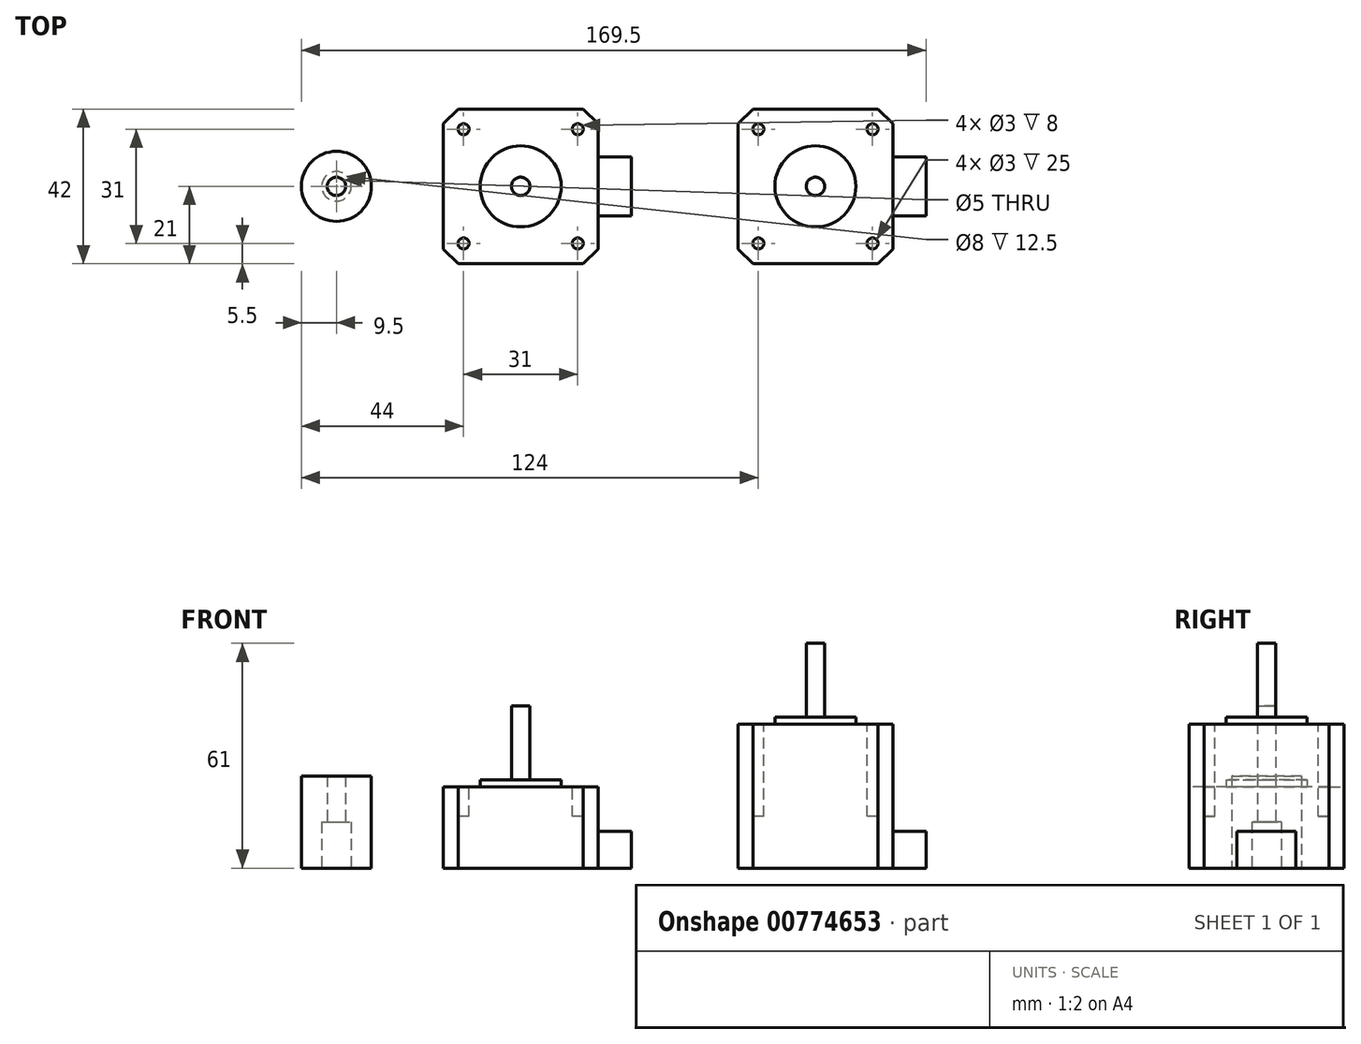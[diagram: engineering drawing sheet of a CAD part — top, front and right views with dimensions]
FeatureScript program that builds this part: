
annotation { "Feature Type Name" : "Feature", "Feature Type Description" : "" }
export const myFeature = defineFeature(function(context is Context, id is Id, definition is map)
    precondition{}
    {
        {
            var Q0;
            Q0=qCreatedBy(makeId("Top.planeOp"),FACE);
            var sketch = newSketch(context, id + "F0", { "sketchPlane" : qUnion([Q0])});
            skLineSegment(sketch, "E0", {"start": v(-21, 17) * mm, "end": v(-21, -17) * mm});
            skLineSegment(sketch, "E1", {"start": v(-21, -17) * mm, "end": v(-17, -21) * mm});
            skLineSegment(sketch, "E2", {"start": v(-17, -21) * mm, "end": v(17, -21) * mm});
            skLineSegment(sketch, "E3", {"start": v(21, -17) * mm, "end": v(17, -21) * mm});
            skLineSegment(sketch, "E4", {"start": v(21, -17) * mm, "end": v(21, 17) * mm});
            skLineSegment(sketch, "E5", {"start": v(21, 17) * mm, "end": v(17, 21) * mm});
            skLineSegment(sketch, "E6", {"start": v(17, 21) * mm, "end": v(-17, 21) * mm});
            skLineSegment(sketch, "E7", {"start": v(-21, 17) * mm, "end": v(-17, 21) * mm});
            skSolve(sketch);
        }
        {
            var Q0;
            Q0=makeQuery(id+"F0.imprint","IMPRINT",FACE,{"disambiguationData":[TD([[makeQuery(id+"F0.imprint","IMPRINT",EDGE,{"derivedFrom":sQuery(id+"F0.wireOp",EDGE,"E0")}),1.0]])]});
            extrude(context, id + "F1", {"entities" : qUnion([Q0]), "depth" : 39 * mm, "offsetDistance" : 25 * mm});
        }
        {
            var Q0;
            Q0=makeQuery(id+"F1.opExtrude","CAP_FACE",FACE,{"disambiguationData":[OSD([sQuery(id+"F0.wireOp",EDGE,"E0"),sQuery(id+"F0.wireOp",EDGE,"E1"),sQuery(id+"F0.wireOp",EDGE,"E2"),sQuery(id+"F0.wireOp",EDGE,"E3"),sQuery(id+"F0.wireOp",EDGE,"E4"),sQuery(id+"F0.wireOp",EDGE,"E5"),sQuery(id+"F0.wireOp",EDGE,"E6"),sQuery(id+"F0.wireOp",EDGE,"E7")])],"isStart":false});
            var sketch = newSketch(context, id + "F2", { "sketchPlane" : qUnion([Q0])});
            skCircle(sketch, "E8", {"center": v(0, 0) * mm, "radius": 11 * mm});
            skSolve(sketch);
        }
        {
            var Q0;
            Q0 = qSketchRegion(id + "F2", true);
            extrude(context, id + "F3", {"entities" : qUnion([Q0]), "operationType" : NewBodyOperationType.ADD, "depth" : 2 * mm, "offsetDistance" : 25 * mm});
        }
        {
            var Q0;
            Q0=makeQuery(id+"F3.opExtrude","CAP_FACE",FACE,{"disambiguationData":[OSD([sQuery(id+"F2.wireOp",EDGE,"E8")])],"isStart":false});
            var sketch = newSketch(context, id + "F4", { "sketchPlane" : qUnion([Q0])});
            skCircle(sketch, "E9", {"center": v(0, 0) * mm, "radius": 2.5 * mm});
            skSolve(sketch);
        }
        {
            var Q0;
            Q0 = qSketchRegion(id + "F4", true);
            extrude(context, id + "F5", {"entities" : qUnion([Q0]), "operationType" : NewBodyOperationType.ADD, "depth" : 20 * mm, "offsetDistance" : 25 * mm});
        }
        {
            var Q0;
            Q0=makeQuery(id+"F1.opExtrude","SWEPT_FACE",FACE,{"disambiguationData":[OSD([sQuery(id+"F0.wireOp",EDGE,"E4")])]});
            var sketch = newSketch(context, id + "F6", { "sketchPlane" : qUnion([Q0])});
            skLineSegment(sketch, "E10.bottom", {"start": v(-8, 0) * mm, "end": v(8, 0) * mm});
            skLineSegment(sketch, "E10.top", {"start": v(-8, 10) * mm, "end": v(8, 10) * mm});
            skLineSegment(sketch, "E10.left", {"start": v(-8, 0) * mm, "end": v(-8, 10) * mm});
            skLineSegment(sketch, "E10.right", {"start": v(8, 0) * mm, "end": v(8, 10) * mm});
            skSolve(sketch);
        }
        {
            var Q0;
            Q0 = qSketchRegion(id + "F6", true);
            extrude(context, id + "F7", {"entities" : qUnion([Q0]), "operationType" : NewBodyOperationType.ADD, "depth" : 9 * mm, "offsetDistance" : 25 * mm});
        }
        {
            var Q0;
            Q0=makeQuery(id+"F1.opExtrude","SWEPT_BODY",BODY,{"disambiguationData":[OSD([sQuery(id+"F0.wireOp",EDGE,"E0"),sQuery(id+"F0.wireOp",EDGE,"E1"),sQuery(id+"F0.wireOp",EDGE,"E2"),sQuery(id+"F0.wireOp",EDGE,"E3"),sQuery(id+"F0.wireOp",EDGE,"E4"),sQuery(id+"F0.wireOp",EDGE,"E5"),sQuery(id+"F0.wireOp",EDGE,"E6"),sQuery(id+"F0.wireOp",EDGE,"E7")])]});
            transform(context, id + "F8", {"entities" : qUnion([Q0]), "transformType" : TransformType.TRANSLATION_3D, "dx" : 82.6 * mm, "dy" : 0 * mm, "dz" : 0 * mm, "makeCopy" : true});
        }
        {
            var Q0;
            Q0=makeQuery(id+"F8.opPattern","COPY",BODY,{"derivedFrom":makeQuery(id+"F1.opExtrude","SWEPT_BODY",BODY,{"disambiguationData":[OSD([sQuery(id+"F0.wireOp",EDGE,"E0"),sQuery(id+"F0.wireOp",EDGE,"E1"),sQuery(id+"F0.wireOp",EDGE,"E2"),sQuery(id+"F0.wireOp",EDGE,"E3"),sQuery(id+"F0.wireOp",EDGE,"E4"),sQuery(id+"F0.wireOp",EDGE,"E5"),sQuery(id+"F0.wireOp",EDGE,"E6"),sQuery(id+"F0.wireOp",EDGE,"E7")])]}),"instanceName":"1"});
            deleteBodies(context, id + "F9", {"entities" : qUnion([Q0])});
        }
        {
            var Q0;
            Q0=makeQuery(id+"F1.opExtrude","SWEPT_BODY",BODY,{"disambiguationData":[OSD([sQuery(id+"F0.wireOp",EDGE,"E0"),sQuery(id+"F0.wireOp",EDGE,"E1"),sQuery(id+"F0.wireOp",EDGE,"E2"),sQuery(id+"F0.wireOp",EDGE,"E3"),sQuery(id+"F0.wireOp",EDGE,"E4"),sQuery(id+"F0.wireOp",EDGE,"E5"),sQuery(id+"F0.wireOp",EDGE,"E6"),sQuery(id+"F0.wireOp",EDGE,"E7")])]});
            var Q1;
            Q1=sQuery(id+"F11.wireOp",EDGE,"E11");
            var Q2;
            Q2=qCreatedBy(makeId("Right.planeOp"),FACE);
            transform(context, id + "F10", {"entities" : qUnion([Q0]), "transformType" : TransformType.TRANSLATION_DISTANCE, "transformDirection" : qUnion([Q2]), "distance" : 80 * mm, "makeCopy" : false});
        }
        {
            var Q0;
            Q0=qCreatedBy(makeId("Top.planeOp"),FACE);
            var sketch = newSketch(context, id + "F11", { "sketchPlane" : qUnion([Q0])});
            skLineSegment(sketch, "E11", {"start": v(-21, 17) * mm, "end": v(-21, -17) * mm});
            skLineSegment(sketch, "E12", {"start": v(-21, -17) * mm, "end": v(-17, -21) * mm});
            skLineSegment(sketch, "E13", {"start": v(-17, -21) * mm, "end": v(17, -21) * mm});
            skLineSegment(sketch, "E14", {"start": v(21, -17) * mm, "end": v(17, -21) * mm});
            skLineSegment(sketch, "E15", {"start": v(21, -17) * mm, "end": v(21, 17) * mm});
            skLineSegment(sketch, "E16", {"start": v(21, 17) * mm, "end": v(17, 21) * mm});
            skLineSegment(sketch, "E17", {"start": v(17, 21) * mm, "end": v(-17, 21) * mm});
            skLineSegment(sketch, "E18", {"start": v(-21, 17) * mm, "end": v(-17, 21) * mm});
            skSolve(sketch);
        }
        {
            var Q0;
            Q0 = qSketchRegion(id + "F11", true);
            extrude(context, id + "F12", {"entities" : qUnion([Q0]), "depth" : 22 * mm, "offsetDistance" : 25 * mm});
        }
        {
            var Q0;
            Q0=makeQuery(id+"F12.opExtrude","CAP_FACE",FACE,{"disambiguationData":[OSD([sQuery(id+"F11.wireOp",EDGE,"E11"),sQuery(id+"F11.wireOp",EDGE,"E12"),sQuery(id+"F11.wireOp",EDGE,"E13"),sQuery(id+"F11.wireOp",EDGE,"E14"),sQuery(id+"F11.wireOp",EDGE,"E15"),sQuery(id+"F11.wireOp",EDGE,"E16"),sQuery(id+"F11.wireOp",EDGE,"E17"),sQuery(id+"F11.wireOp",EDGE,"E18")])],"isStart":false});
            var sketch = newSketch(context, id + "F13", { "sketchPlane" : qUnion([Q0])});
            skCircle(sketch, "E19", {"center": v(0, 0) * mm, "radius": 11 * mm});
            skSolve(sketch);
        }
        {
            var Q0;
            Q0 = qSketchRegion(id + "F13", true);
            var Q1;
            Q1=sQuery(id+"F13.wireOp",EDGE,"E19");
            extrude(context, id + "F14", {"entities" : qUnion([Q0]), "operationType" : NewBodyOperationType.ADD, "surfaceEntities" : qUnion([Q1]), "depth" : 2 * mm, "offsetDistance" : 25 * mm});
        }
        {
            var Q0;
            Q0=makeQuery(id+"F14.opExtrude","CAP_FACE",FACE,{"disambiguationData":[OSD([sQuery(id+"F13.wireOp",EDGE,"E19")])],"isStart":false});
            var sketch = newSketch(context, id + "F15", { "sketchPlane" : qUnion([Q0])});
            skCircle(sketch, "E20", {"center": v(0, 0) * mm, "radius": 2.5 * mm});
            skSolve(sketch);
        }
        {
            var Q0;
            Q0 = qSketchRegion(id + "F15", true);
            extrude(context, id + "F16", {"entities" : qUnion([Q0]), "operationType" : NewBodyOperationType.ADD, "depth" : 20 * mm, "offsetDistance" : 25 * mm});
        }
        {
            var Q0;
            Q0=makeQuery(id+"F12.opExtrude","SWEPT_FACE",FACE,{"disambiguationData":[OSD([sQuery(id+"F11.wireOp",EDGE,"E15")])]});
            var sketch = newSketch(context, id + "F17", { "sketchPlane" : qUnion([Q0])});
            skLineSegment(sketch, "E21.bottom", {"start": v(-8, 0) * mm, "end": v(8, 0) * mm});
            skLineSegment(sketch, "E21.top", {"start": v(-8, 10) * mm, "end": v(8, 10) * mm});
            skLineSegment(sketch, "E21.left", {"start": v(-8, 0) * mm, "end": v(-8, 10) * mm});
            skLineSegment(sketch, "E21.right", {"start": v(8, 0) * mm, "end": v(8, 10) * mm});
            skSolve(sketch);
        }
        {
            var Q0;
            Q0 = qSketchRegion(id + "F17", true);
            extrude(context, id + "F18", {"entities" : qUnion([Q0]), "operationType" : NewBodyOperationType.ADD, "depth" : 9 * mm, "offsetDistance" : 25 * mm});
        }
        {
            var Q0;
            Q0=qCreatedBy(makeId("Top.planeOp"),FACE);
            var sketch = newSketch(context, id + "F19", { "sketchPlane" : qUnion([Q0])});
            skCircle(sketch, "E22", {"center": v(-50, 0) * mm, "radius": 2.5 * mm});
            skCircle(sketch, "E23", {"center": v(-50, 0) * mm, "radius": 9.5 * mm});
            skSolve(sketch);
        }
        {
            var Q0;
            Q0=makeQuery(id+"F19.imprint","IMPRINT",FACE,{"disambiguationData":[TD([[makeQuery(id+"F19.imprint","IMPRINT",EDGE,{"derivedFrom":sQuery(id+"F19.wireOp",EDGE,"E22")}),-1.0]])]});
            extrude(context, id + "F20", {"entities" : qUnion([Q0]), "depth" : 25 * mm, "offsetDistance" : 25 * mm});
        }
        {
            var Q0;
            Q0=makeQuery(id+"F20.opExtrude","CAP_FACE",FACE,{"disambiguationData":[OSD([sQuery(id+"F19.wireOp",EDGE,"E22"),sQuery(id+"F19.wireOp",EDGE,"E23")])],"isStart":true});
            var sketch = newSketch(context, id + "F21", { "sketchPlane" : qUnion([Q0])});
            skCircle(sketch, "E24", {"center": v(-50, 0) * mm, "radius": 4 * mm});
            skSolve(sketch);
        }
        {
            var Q0;
            Q0 = qSketchRegion(id + "F21", true);
            extrude(context, id + "F22", {"entities" : qUnion([Q0]), "operationType" : NewBodyOperationType.REMOVE, "oppositeDirection" : true, "depth" : 12.5 * mm, "offsetDistance" : 25 * mm});
        }
        {
            var Q0;
            Q0=makeQuery(id+"F1.opExtrude","CAP_FACE",FACE,{"disambiguationData":[OSD([sQuery(id+"F0.wireOp",EDGE,"E0"),sQuery(id+"F0.wireOp",EDGE,"E1"),sQuery(id+"F0.wireOp",EDGE,"E2"),sQuery(id+"F0.wireOp",EDGE,"E3"),sQuery(id+"F0.wireOp",EDGE,"E4"),sQuery(id+"F0.wireOp",EDGE,"E5"),sQuery(id+"F0.wireOp",EDGE,"E6"),sQuery(id+"F0.wireOp",EDGE,"E7")])],"isStart":false});
            var sketch = newSketch(context, id + "F23", { "sketchPlane" : qUnion([Q0])});
            skCircle(sketch, "E25", {"center": v(-15.5, 15.5) * mm, "radius": 1.5 * mm});
            skCircle(sketch, "E26", {"center": v(15.5, 15.5) * mm, "radius": 1.5 * mm});
            skCircle(sketch, "E27", {"center": v(15.5, -15.5) * mm, "radius": 1.5 * mm});
            skCircle(sketch, "E28", {"center": v(-15.5, -15.5) * mm, "radius": 1.5 * mm});
            skCircle(sketch, "E29", {"center": v(64.5, -15.5) * mm, "radius": 1.5 * mm});
            skCircle(sketch, "E30", {"center": v(64.5, 15.5) * mm, "radius": 1.5 * mm});
            skCircle(sketch, "E31", {"center": v(95.5, 15.5) * mm, "radius": 1.5 * mm});
            skCircle(sketch, "E32", {"center": v(95.5, -15.5) * mm, "radius": 1.5 * mm});
            skLineSegment(sketch, "E33", {"start": v(-35.11, -15.5) * mm, "end": v(115.72, -15.5) * mm, "construction": true});
            skLineSegment(sketch, "E34", {"start": v(-35.11, 15.5) * mm, "end": v(121.76, 15.5) * mm, "construction": true});
            skLineSegment(sketch, "E35", {"start": v(-15.5, 41.42) * mm, "end": v(-15.5, -36.89) * mm, "construction": true});
            skLineSegment(sketch, "E36", {"start": v(15.5, 40.29) * mm, "end": v(15.5, -36.89) * mm, "construction": true});
            skLineSegment(sketch, "E37", {"start": v(64.5, 39.15) * mm, "end": v(64.5, -37.64) * mm, "construction": true});
            skLineSegment(sketch, "E38", {"start": v(95.5, 49.73) * mm, "end": v(95.5, -37.64) * mm, "construction": true});
            skLineSegment(sketch, "E39", {"start": v(80, 41.42) * mm, "end": v(80, -38.4) * mm, "construction": true});
            skCircle(sketch, "E40", {"center": v(80, 0) * mm, "radius": 2.5 * mm, "construction": true});
            skSolve(sketch);
        }
        {
            var Q0;
            Q0 = qSketchRegion(id + "F23", true);
            extrude(context, id + "F24", {"entities" : qUnion([Q0]), "operationType" : NewBodyOperationType.REMOVE, "oppositeDirection" : true, "depth" : 25 * mm, "offsetDistance" : 25 * mm});
        }
    });
